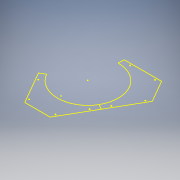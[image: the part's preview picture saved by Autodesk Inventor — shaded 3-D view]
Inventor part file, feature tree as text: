
AUTODESK INVENTOR PART (.ipt)
format: ipt  version: 2016 SP1 (Build 200210100, 210)  size: 93,696 bytes
history: native  units: mm
features: extrude x1, sketch x1
ambient origin geometry x8: Origin, YZ Plane, XZ Plane, XY Plane, X Axis, Y Axis, Z Axis, Center Point
bodies: Solid1 (feature_tree)
feature tree (2):
  extrude  "Extrusion1"  [1 undecoded]
  sketch  "Sketch1"  dims[d0=3.0mm d1=0.0mm]
note: 1 required parameter value undecoded (feature->parameter linkage not recoverable at this tier; creation-order binding heuristic only, values carry confidence <= 0.55)
